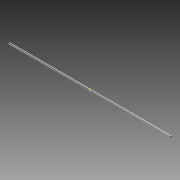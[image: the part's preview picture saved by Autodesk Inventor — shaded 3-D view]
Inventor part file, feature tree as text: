
AUTODESK INVENTOR PART (.ipt)
format: ipt  version: 2015 (Build 190159000, 159)  size: 70,656 bytes
history: native  units: mm
features: revolve x1, chamfer x1
ambient origin geometry x8: Origin, YZ Plane, XZ Plane, XY Plane, X Axis, Y Axis, Z Axis, Center Point
bodies: Solid1 (feature_tree)
feature tree (2):
  revolve  "Revolución1"  [1 undecoded]
  chamfer  "Chaflán1"  Distance=487.0mm
note: 1 required parameter value undecoded (feature->parameter linkage not recoverable at this tier; creation-order binding heuristic only, values carry confidence <= 0.55)
